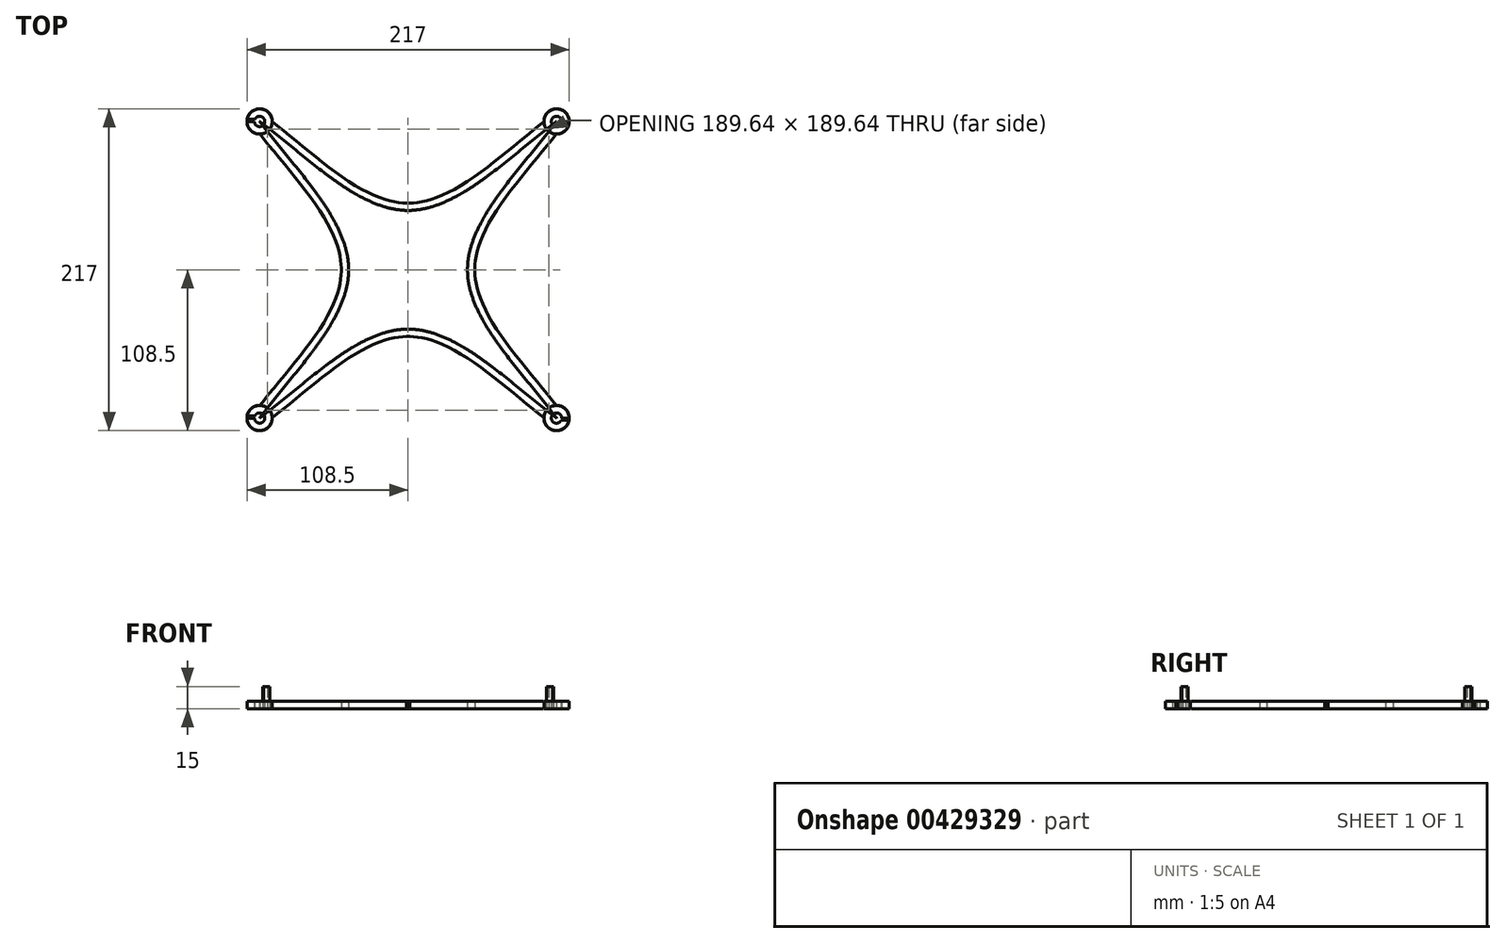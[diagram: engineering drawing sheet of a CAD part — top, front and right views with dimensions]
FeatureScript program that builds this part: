
annotation { "Feature Type Name" : "Feature", "Feature Type Description" : "" }
export const myFeature = defineFeature(function(context is Context, id is Id, definition is map)
    precondition{}
    {
        {
            var Q0;
            Q0=qCreatedBy(makeId("Top.planeOp"),FACE);
            var sketch = newSketch(context, id + "F0", { "sketchPlane" : qUnion([Q0])});
            skPoint(sketch, "E0.middle", {"position": v(0, 0) * mm});
            skFitSpline(sketch, "E1", {"points": [v(-100, 100) * mm, v(-40, 0) * mm, v(-100, -100) * mm], "startDerivative": vector(150, -200) * mm, "endDerivative": vector(-150, -200) * mm});
            skFitSpline(sketch, "E2", {"points": [v(100, 100) * mm, v(40, 0) * mm, v(100, -100) * mm], "startDerivative": vector(-150, -200) * mm, "endDerivative": vector(150, -200) * mm});
            skFitSpline(sketch, "E3", {"points": [v(-100, 100) * mm, v(0, 40) * mm, v(100, 100) * mm], "startDerivative": vector(200, -150) * mm, "endDerivative": vector(200, 150) * mm});
            skFitSpline(sketch, "E4.0", {"points": [v(104, 97) * mm, v(100.83, 92.77) * mm, v(94.2, 84.35) * mm, v(83.92, 71.82) * mm, v(73.84, 59.4) * mm, v(64.49, 47.07) * mm, v(56.39, 34.9) * mm, v(51.12, 24.93) * mm, v(48.02, 17.1) * mm, v(46.3, 11.31) * mm, v(45.42, 6.56) * mm, v(45.06, 2.8) * mm, v(44.97, 0) * mm, v(45.06, -2.8) * mm, v(45.42, -6.56) * mm, v(46.3, -11.31) * mm, v(48.02, -17.1) * mm, v(51.12, -24.93) * mm, v(56.39, -34.9) * mm, v(64.49, -47.07) * mm, v(73.84, -59.4) * mm, v(83.92, -71.82) * mm, v(94.2, -84.35) * mm, v(100.83, -92.77) * mm, v(104, -97) * mm]});
            skFitSpline(sketch, "E5.0", {"points": [v(-97, 104) * mm, v(-92.77, 100.83) * mm, v(-84.35, 94.2) * mm, v(-71.82, 83.92) * mm, v(-59.4, 73.84) * mm, v(-47.07, 64.49) * mm, v(-34.9, 56.39) * mm, v(-24.93, 51.12) * mm, v(-17.1, 48.02) * mm, v(-11.31, 46.3) * mm, v(-6.56, 45.42) * mm, v(-2.8, 45.06) * mm, v(0, 44.97) * mm, v(2.8, 45.06) * mm, v(6.56, 45.42) * mm, v(11.31, 46.3) * mm, v(17.1, 48.02) * mm, v(24.93, 51.12) * mm, v(34.9, 56.39) * mm, v(47.07, 64.49) * mm, v(59.4, 73.84) * mm, v(71.82, 83.92) * mm, v(84.35, 94.2) * mm, v(92.77, 100.83) * mm, v(97, 104) * mm]});
            skFitSpline(sketch, "E6.0", {"points": [v(-104, 97) * mm, v(-100.83, 92.77) * mm, v(-94.2, 84.35) * mm, v(-83.92, 71.82) * mm, v(-73.84, 59.4) * mm, v(-64.49, 47.07) * mm, v(-56.39, 34.9) * mm, v(-51.12, 24.93) * mm, v(-48.02, 17.1) * mm, v(-46.3, 11.31) * mm, v(-45.42, 6.56) * mm, v(-45.06, 2.8) * mm, v(-44.97, 0) * mm, v(-45.06, -2.8) * mm, v(-45.42, -6.56) * mm, v(-46.3, -11.31) * mm, v(-48.02, -17.1) * mm, v(-51.12, -24.93) * mm, v(-56.39, -34.9) * mm, v(-64.49, -47.07) * mm, v(-73.84, -59.4) * mm, v(-83.92, -71.82) * mm, v(-94.2, -84.35) * mm, v(-100.83, -92.77) * mm, v(-104, -97) * mm]});
            skFitSpline(sketch, "E7.0", {"points": [v(-97, -104) * mm, v(-92.77, -100.83) * mm, v(-84.35, -94.2) * mm, v(-71.82, -83.92) * mm, v(-59.4, -73.84) * mm, v(-47.07, -64.49) * mm, v(-34.9, -56.39) * mm, v(-24.93, -51.12) * mm, v(-17.1, -48.02) * mm, v(-11.31, -46.3) * mm, v(-6.56, -45.42) * mm, v(-2.8, -45.06) * mm, v(0, -44.97) * mm, v(2.8, -45.06) * mm, v(6.56, -45.42) * mm, v(11.31, -46.3) * mm, v(17.1, -48.02) * mm, v(24.93, -51.12) * mm, v(34.9, -56.39) * mm, v(47.07, -64.49) * mm, v(59.4, -73.84) * mm, v(71.82, -83.92) * mm, v(84.35, -94.2) * mm, v(92.77, -100.83) * mm, v(97, -104) * mm]});
            skCircle(sketch, "E8", {"center": v(0, 0) * mm, "radius": 40 * mm});
            skCircle(sketch, "E9.0", {"center": v(0, 0) * mm, "radius": 45 * mm});
            skArc(sketch, "E10", {"start": v(-103.5, 100) * mm, "mid": v(-96.59, 99.23) * mm, "end": v(-103.16, 101.5) * mm});
            skArc(sketch, "E11.0", {"start": v(-108.5, 100) * mm, "mid": v(-91.53, 99.25) * mm, "end": v(-108.37, 101.5) * mm});
            skLineSegment(sketch, "E12", {"start": v(-103.5, 100) * mm, "end": v(-108.5, 100) * mm});
            skLineSegment(sketch, "E13.0", {"start": v(-103.16, 101.5) * mm, "end": v(-108.37, 101.5) * mm});
            skArc(sketch, "E14", {"start": v(-103.5, -100) * mm, "mid": v(-96.59, -100.77) * mm, "end": v(-103.16, -98.5) * mm});
            skArc(sketch, "E15.0", {"start": v(-108.5, -100) * mm, "mid": v(-91.53, -100.75) * mm, "end": v(-108.37, -98.5) * mm});
            skLineSegment(sketch, "E16", {"start": v(-103.5, -100) * mm, "end": v(-108.5, -100) * mm});
            skLineSegment(sketch, "E17.0", {"start": v(-103.16, -98.5) * mm, "end": v(-108.37, -98.5) * mm});
            skArc(sketch, "E18", {"start": v(103.5, 100) * mm, "mid": v(96.59, 100.77) * mm, "end": v(103.16, 98.5) * mm});
            skArc(sketch, "E19.0", {"start": v(108.5, 100) * mm, "mid": v(91.53, 100.75) * mm, "end": v(108.37, 98.5) * mm});
            skLineSegment(sketch, "E20", {"start": v(103.5, 100) * mm, "end": v(108.5, 100) * mm});
            skLineSegment(sketch, "E21.0", {"start": v(103.16, 98.5) * mm, "end": v(108.37, 98.5) * mm});
            skArc(sketch, "E22", {"start": v(103.5, -100) * mm, "mid": v(96.59, -99.23) * mm, "end": v(103.16, -101.5) * mm});
            skArc(sketch, "E23.0", {"start": v(108.5, -100) * mm, "mid": v(91.53, -99.25) * mm, "end": v(108.37, -101.5) * mm});
            skLineSegment(sketch, "E24", {"start": v(103.5, -100) * mm, "end": v(108.5, -100) * mm});
            skLineSegment(sketch, "E25.0", {"start": v(103.16, -101.5) * mm, "end": v(108.37, -101.5) * mm});
            skFitSpline(sketch, "E26.trimOffspring", {"points": [v(-100, -100) * mm, v(0, -40) * mm, v(100, -100) * mm], "startDerivative": vector(200, 150) * mm, "endDerivative": vector(200, -150) * mm});
            skLineSegment(sketch, "E27", {"start": v(-50, 33.33) * mm, "end": v(-33.33, 50) * mm});
            skLineSegment(sketch, "E28", {"start": v(33.33, 50) * mm, "end": v(50, 33.33) * mm});
            skLineSegment(sketch, "E29", {"start": v(-50, -33.33) * mm, "end": v(-33.33, -50) * mm});
            skLineSegment(sketch, "E30", {"start": v(33.33, -50) * mm, "end": v(50, -33.33) * mm});
            skLineSegment(sketch, "E31", {"start": v(-62.5, 52.6) * mm, "end": v(-52.6, 62.5) * mm});
            skLineSegment(sketch, "E32", {"start": v(52.6, 62.5) * mm, "end": v(62.5, 52.6) * mm});
            skLineSegment(sketch, "E33", {"start": v(62.5, -52.6) * mm, "end": v(52.6, -62.5) * mm});
            skLineSegment(sketch, "E34", {"start": v(-52.6, -62.5) * mm, "end": v(-62.5, -52.6) * mm});
            skLineSegment(sketch, "E35.0", {"start": v(-65.52, 56.65) * mm, "end": v(-56.65, 65.52) * mm});
            skLineSegment(sketch, "E36.0", {"start": v(-52.58, 37.82) * mm, "end": v(-37.82, 52.58) * mm});
            skLineSegment(sketch, "E37.0", {"start": v(37.82, 52.58) * mm, "end": v(52.58, 37.82) * mm});
            skLineSegment(sketch, "E38.0", {"start": v(56.65, 65.52) * mm, "end": v(65.52, 56.65) * mm});
            skLineSegment(sketch, "E39.0", {"start": v(37.82, -52.58) * mm, "end": v(52.58, -37.82) * mm});
            skLineSegment(sketch, "E40.0", {"start": v(65.52, -56.65) * mm, "end": v(56.65, -65.52) * mm});
            skLineSegment(sketch, "E41.0", {"start": v(-52.58, -37.82) * mm, "end": v(-37.82, -52.58) * mm});
            skLineSegment(sketch, "E42.0", {"start": v(-56.65, -65.52) * mm, "end": v(-65.52, -56.65) * mm});
            skSolve(sketch);
        }
        {
            var Q0;
            Q0=makeQuery(id+"F0.imprint","IMPRINT",FACE,{"disambiguationData":[TD([[makeQuery(id+"F0.imprint","IMPRINT",EDGE,{"derivedFrom":sQuery(id+"F0.wireOp",EDGE,"E10")}),-1.0]])]});
            var Q1;
            Q1=makeQuery(id+"F0.imprint","IMPRINT",FACE,{"disambiguationData":[TD([[makeQuery(id+"F0.imprint","IMPRINT",EDGE,{"derivedFrom":sQuery(id+"F0.wireOp",EDGE,"E18")}),-1.0]])]});
            var Q2;
            Q2=makeQuery(id+"F0.imprint","IMPRINT",FACE,{"disambiguationData":[TD([[makeQuery(id+"F0.imprint","IMPRINT",EDGE,{"derivedFrom":sQuery(id+"F0.wireOp",EDGE,"E22")}),-1.0]])]});
            var Q3;
            Q3=makeQuery(id+"F0.imprint","IMPRINT",FACE,{"disambiguationData":[TD([[makeQuery(id+"F0.imprint","IMPRINT",EDGE,{"derivedFrom":sQuery(id+"F0.wireOp",EDGE,"E14")}),-1.0]])]});
            extrude(context, id + "F1", {"entities" : qUnion([Q0, Q1, Q2, Q3]), "depth" : 15 * mm});
        }
        {
            var Q0;
            Q0 = qSketchRegion(id + "F0", true);
            extrude(context, id + "F2", {"entities" : qUnion([Q0]), "depth" : 5 * mm});
        }
    });
